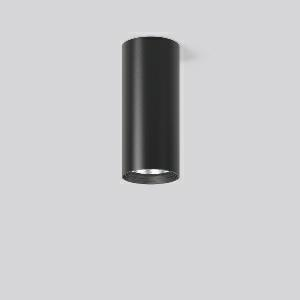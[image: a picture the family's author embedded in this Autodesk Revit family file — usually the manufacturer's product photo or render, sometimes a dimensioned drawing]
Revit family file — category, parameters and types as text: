
# Revit family: heledon_mini_a_931201_003_7c57
name_source: partatom
category: Lighting Fixtures
units: mm (PartAtom-declared; Revit-internal decimal feet)

## family parameters
Cut with Voids When Loaded = No
Host = Face
Light Source = No
Part Type = Normal
Room Calculation Point = No
Round Connector Dimension = Use Diameter
Shared = No

## types (1)
- HELEDON mini A (1 x LED Modul 930, 2450 lm, 3000)
    Apparent Load = 20 VA
    Approval mark = CE
    CIE Flux Codes = 99 100 100 100 100
    Color Rendering = 90
    Color Temperature = 3000
    Default Elevation = 1800 mm
    Description = Series: HELEDON mini
Cylindrical surface-mounted downlight. Housing: die-cast aluminium, powder-coated. Internal ceiling frame polycarbonate with bayonet mounting. Black plastic ring and recessed LED to prevent glare from the side. Optical assembly with reflector made of MIRO-Silver with 98% total light reflection for outstanding efficiency - can be changed without tools. Best colour rendering index Ra>90. Suitable for Ceiling mounting. Easy installation with a separate ceiling frame with bayonet mounting and plug connection. Driver integrated. Connected via plug-in connector. High quality converter without flickering and stroboscopic effect. The following accessories can be mounted without use of tools: interchangeable lenses, decorative glasses, honeycomb louvre, clear and frosted diffusers, white interchangeable plastic ring. 
Colour: deep black, matt (RAL 9005)
Diameter: 87 mm
Height: 197 mm
Lamp: LED
Socket: without socket
Colour temperature: 3000K
Colour rendering index (CRI): 92
System power: 20 W
Rated luminous flux: 2450 lm
Luminous efficiency: 123 lm/W
Control gear: Regulated power supply
Protection class: I
Type of protection: IP 20
    Height = 197 mm
    Lamp = 1 x LED Modul 930
    Lamp Light Flux = 2450 lm
    Lamp count = 1
    Length = 87 mm
    Lifetime = 50000 h
    Luminous efficacy = 123 lm/W
    Manufacturer = RZB
    ModVariant = No
    Model = 931201.003
    Mounting Place = Ceiling
    Mounting Type = Surface mounted
    Number of Poles = 1
    OnlyDefault = Yes
    Power Factor = 1
    Product Name = HELEDON mini A
    Product group = Surface mounted downlights
    ProductGroupID = 302
    Protection Class = Protection class I
    Protection Degree = IP 20
    RLX_Detail_Level = 1
    RLX_Emergency_Light_Flux = 0 lm
    RLX_Emergency_Type = 0
    RLX_Emergency_Type_DB = No
    RlxData = <blob elided: 104441 chars, md5=7b91cd6d>
    Socket = socket
    Standby Power = 0 W
    System Light Flux = 2450 lm
    System Power = 20 W
    Type Comments = Product without accessories
    Type Image = 931188.003.jpg
    URL = http://relux.com
    VarID = ---
    Voltage = 230 V
    Voltage Range = 220-240 V
    Weight = 0.00 kg
    Width = 0 mm  [stored 0 ft]

note: [stored X ft] marks values corroborated as IEEE doubles in the binary element streams (Revit-internal decimal feet)

## geometry (parser evidence)
native form markers: Blend x4, Sweep x9
no freeform markers — native parametric forms only
